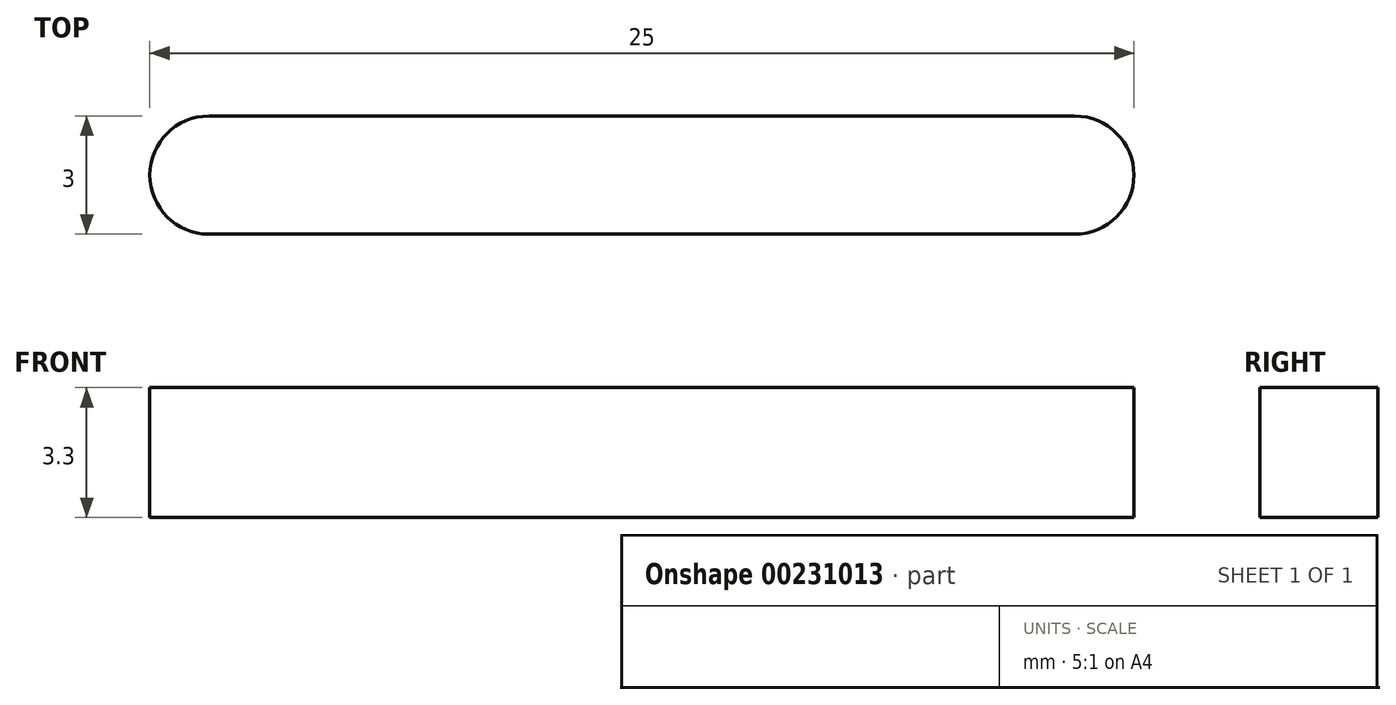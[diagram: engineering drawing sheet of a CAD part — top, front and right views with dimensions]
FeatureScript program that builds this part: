
annotation { "Feature Type Name" : "Feature", "Feature Type Description" : "" }
export const myFeature = defineFeature(function(context is Context, id is Id, definition is map)
    precondition{}
    {
        {
            var Q0;
            Q0=qCreatedBy(makeId("Top.planeOp"),FACE);
            var sketch = newSketch(context, id + "F0", { "sketchPlane" : qUnion([Q0])});
            skLineSegment(sketch, "E0.bottom", {"start": v(1.5, 0) * mm, "end": v(23.5, 0) * mm});
            skLineSegment(sketch, "E0.top", {"start": v(1.5, 3) * mm, "end": v(23.5, 3) * mm});
            skLineSegment(sketch, "E0.left", {"start": v(0, 1.5) * mm, "end": v(0, 1.5) * mm});
            skLineSegment(sketch, "E0.right", {"start": v(25, 1.5) * mm, "end": v(25, 1.5) * mm});
            skPoint(sketch, "E1.visualSharp", {"position": v(0, 3) * mm});
            skArc(sketch, "E1.filletArc", {"start": v(1.5, 3) * mm, "mid": v(0.44, 2.56) * mm, "end": v(0, 1.5) * mm});
            skPoint(sketch, "E2.visualSharp", {"position": v(0, 0) * mm});
            skArc(sketch, "E2.filletArc", {"start": v(0, 1.5) * mm, "mid": v(0.44, 0.44) * mm, "end": v(1.5, 0) * mm});
            skPoint(sketch, "E3.visualSharp", {"position": v(25, 3) * mm});
            skArc(sketch, "E3.filletArc", {"start": v(25, 1.5) * mm, "mid": v(24.56, 2.56) * mm, "end": v(23.5, 3) * mm});
            skPoint(sketch, "E4.visualSharp", {"position": v(25, 0) * mm});
            skArc(sketch, "E4.filletArc", {"start": v(23.5, 0) * mm, "mid": v(24.56, 0.44) * mm, "end": v(25, 1.5) * mm});
            skSolve(sketch);
        }
        {
            var Q0;
            Q0=makeQuery(id+"F0.imprint","IMPRINT",FACE,{"disambiguationData":[TD([[makeQuery(id+"F0.imprint","IMPRINT",EDGE,{"derivedFrom":sQuery(id+"F0.wireOp",EDGE,"E0.bottom")}),1.0]])]});
            extrude(context, id + "F1", {"entities" : qUnion([Q0]), "depth" : 3.3 * mm});
        }
    });
